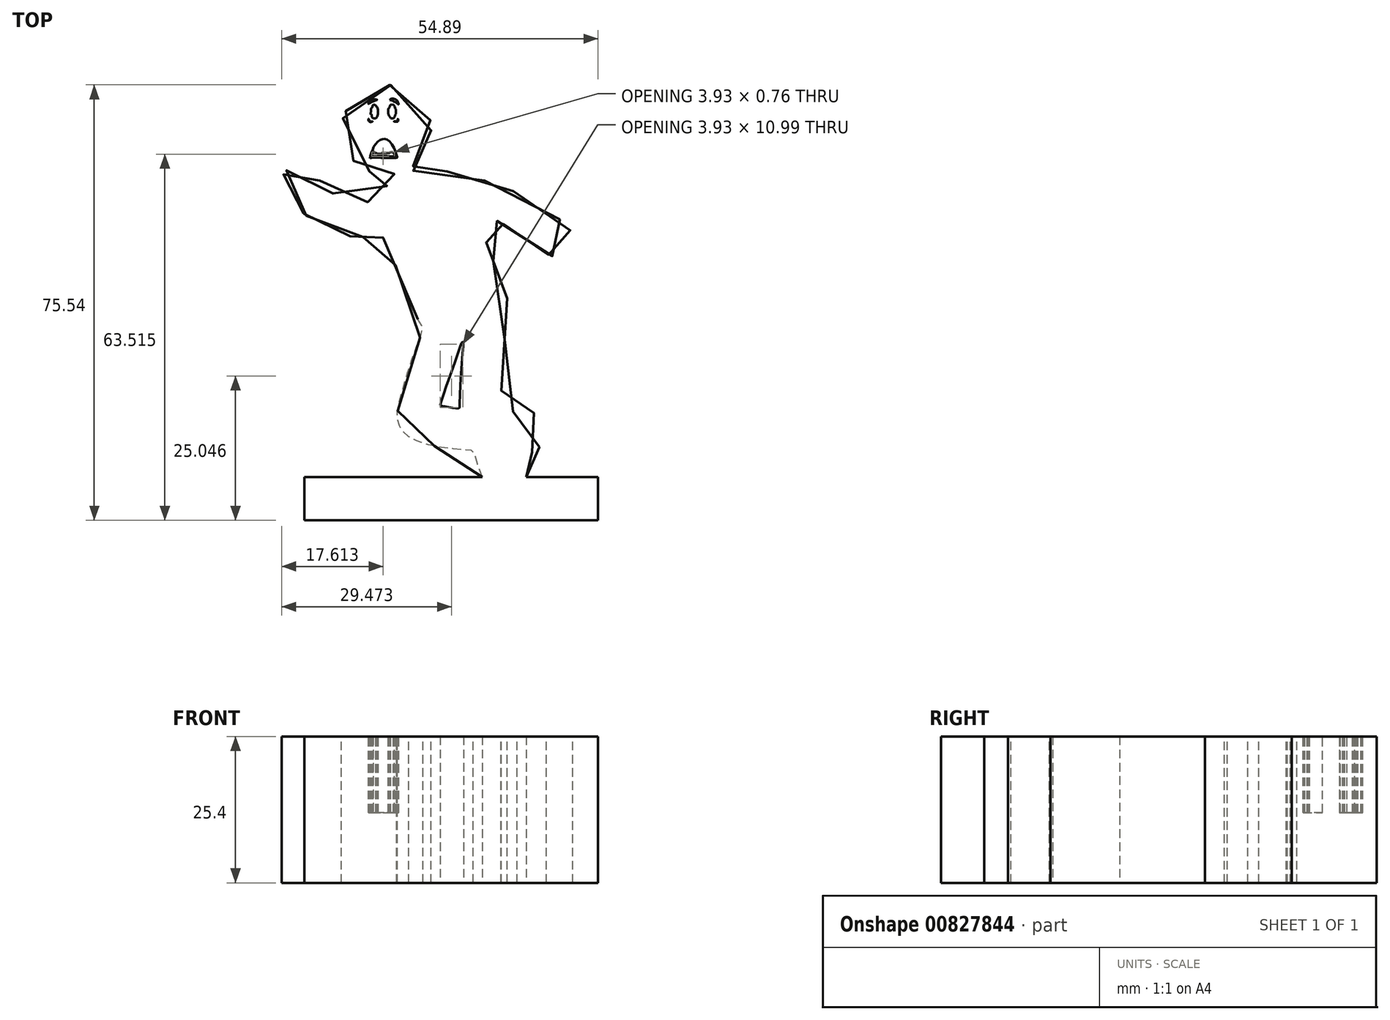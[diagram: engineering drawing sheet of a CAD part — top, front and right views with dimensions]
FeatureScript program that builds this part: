
annotation { "Feature Type Name" : "Feature", "Feature Type Description" : "" }
export const myFeature = defineFeature(function(context is Context, id is Id, definition is map)
    precondition{}
    {
        {
            var Q0;
            Q0=qCreatedBy(makeId("Top.planeOp"),FACE);
            var sketch = newSketch(context, id + "F0", { "sketchPlane" : qUnion([Q0])});
            skFitSpline(sketch, "E0", {"points": [v(-34.43, 17.8) * mm, v(-33.8, 19.88) * mm, v(-32.72, 23) * mm, v(-31.12, 27.5) * mm, v(-30.7, 28.65) * mm, v(-30.46, 28.82) * mm, v(-30.5, 27.56) * mm, v(-30.92, 21.8) * mm, v(-31.06, 17.6) * mm, v(-31.12, 17.25) * mm, v(-31.55, 17.25) * mm, v(-34.17, 17.65) * mm, v(-34.46, 17.72) * mm, v(-34.45, 17.74) * mm, v(-34.43, 17.78) * mm, v(-34.43, 17.8) * mm]});
            skFitSpline(sketch, "E1", {"points": [v(-21.09, 9.56) * mm, v(-20.18, 7) * mm, v(-19.25, 4.29) * mm, v(-19.41, 2.26) * mm, v(-20.88, 0.48) * mm, v(-22.42, 0) * mm, v(-24.42, 0.37) * mm, v(-25.78, 1.51) * mm, v(-26.8, 4.26) * mm, v(-28.3, 8.68) * mm, v(-28.7, 9.9) * mm, v(-29.32, 9.99) * mm, v(-31.53, 10.19) * mm, v(-35.27, 10.68) * mm, v(-38.95, 11.8) * mm, v(-40.4, 12.75) * mm, v(-41.25, 13.76) * mm, v(-41.78, 15.03) * mm, v(-41.86, 16.4) * mm, v(-41.72, 17.56) * mm, v(-40.92, 20.58) * mm, v(-40.26, 22.95) * mm, v(-38.55, 27.93) * mm, v(-37.54, 30.8) * mm, v(-37.48, 31.16) * mm, v(-37.45, 31.38) * mm, v(-37.89, 31.95) * mm, v(-38.71, 33.7) * mm, v(-42.6, 43) * mm, v(-44.25, 46.66) * mm, v(-44.57, 47.49) * mm, v(-44.86, 47.49) * mm, v(-45.4, 47.38) * mm, v(-45.94, 47.24) * mm, v(-46.3, 47.1) * mm, v(-48.1, 46.98) * mm, v(-50.44, 47.16) * mm, v(-52.24, 47.63) * mm, v(-53.94, 48.3) * mm, v(-56.24, 49.65) * mm, v(-58.44, 51.35) * mm, v(-60.2, 53.34) * mm, v(-61.6, 55.05) * mm, v(-61.87, 56) * mm, v(-61.87, 57.27) * mm, v(-61.11, 58.54) * mm, v(-60.17, 59.28) * mm, v(-58.54, 59.53) * mm, v(-57.12, 59.05) * mm, v(-55.31, 56.76) * mm, v(-53.1, 54.57) * mm, v(-51.22, 53.6) * mm, v(-49.05, 53.02) * mm, v(-46.71, 53.1) * mm, v(-45, 54.06) * mm, v(-43.3, 56.33) * mm, v(-42.57, 56.9) * mm, v(-41.97, 57.34) * mm, v(-42.34, 57.9) * mm, v(-42.55, 57.82) * mm, v(-43.4, 57.75) * mm, v(-45.08, 57.84) * mm, v(-46.6, 58.3) * mm, v(-48.82, 59.6) * mm, v(-50.7, 61.94) * mm, v(-51.53, 64.44) * mm, v(-51.5, 66.62) * mm, v(-51.06, 68.33) * mm, v(-49.91, 70.34) * mm, v(-48.04, 72.06) * mm, v(-46.07, 73) * mm, v(-43.55, 73.38) * mm, v(-41.12, 72.92) * mm, v(-38.67, 71.45) * mm, v(-36.76, 69.07) * mm, v(-36.06, 66.72) * mm, v(-36.04, 64.75) * mm, v(-36.33, 63.02) * mm, v(-37.79, 60.48) * mm, v(-39.33, 59.1) * mm, v(-39.87, 58.8) * mm, v(-39.36, 58.42) * mm, v(-38.99, 58.51) * mm, v(-37.05, 58.68) * mm, v(-34.13, 58.51) * mm, v(-30.46, 57.82) * mm, v(-26.68, 56.71) * mm, v(-23, 55.43) * mm, v(-18.6, 53.35) * mm, v(-14.93, 50.93) * mm, v(-12.28, 48.7) * mm, v(-11.48, 46.97) * mm, v(-11.89, 45.14) * mm, v(-12.8, 44.16) * mm, v(-13.4, 43.82) * mm, v(-15, 43.68) * mm, v(-16.8, 44.7) * mm, v(-18.07, 45.77) * mm, v(-19.6, 46.97) * mm, v(-22.71, 48.83) * mm, v(-26.07, 50.36) * mm, v(-28.44, 50.98) * mm, v(-28.72, 50.98) * mm, v(-26.78, 46.83) * mm, v(-25.17, 42.6) * mm, v(-23.84, 39.69) * mm, v(-22.87, 37.29) * mm, v(-22.92, 35.57) * mm, v(-23.36, 27.21) * mm, v(-23.86, 20.33) * mm, v(-23.86, 18.27) * mm, v(-23.61, 16.9) * mm, v(-21.3, 16.74) * mm, v(-18.45, 16.55) * mm, v(-16.53, 15.02) * mm, v(-16, 12.96) * mm, v(-16.4, 11.47) * mm, v(-18.02, 9.96) * mm, v(-19.27, 9.44) * mm, v(-20.16, 9.54) * mm, v(-20.78, 9.55) * mm, v(-20.97, 9.58) * mm, v(-21.03, 9.58) * mm, v(-21.09, 9.56) * mm]});
            skSolve(sketch);
        }
        {
            var Q0;
            Q0=makeQuery(id+"F0.imprint","IMPRINT",FACE,{"disambiguationData":[TD([[makeQuery(id+"F0.imprint","IMPRINT",EDGE,{"derivedFrom":sQuery(id+"F0.wireOp",EDGE,"E0")}),1.0]])]});
            extrude(context, id + "F1", {"entities" : qUnion([Q0]), "depth" : 25.4 * mm, "offsetDistance" : 25.4 * mm});
        }
        {
            var Q0;
            Q0=makeQuery(id+"F1.opExtrude","CAP_FACE",FACE,{"disambiguationData":[OSD([sQuery(id+"F0.wireOp",EDGE,"E0"),sQuery(id+"F0.wireOp",EDGE,"E1")])],"isStart":false});
            var sketch = newSketch(context, id + "F2", { "sketchPlane" : qUnion([Q0])});
            skFitSpline(sketch, "E2", {"points": [v(-46.89, 70.28) * mm, v(-46.68, 70.57) * mm, v(-46.42, 70.8) * mm, v(-45.95, 70.9) * mm, v(-45.37, 70.78) * mm, v(-45.59, 70.7) * mm, v(-45.92, 70.58) * mm, v(-46.42, 70.37) * mm, v(-46.7, 70.18) * mm, v(-46.8, 70.18) * mm, v(-46.84, 70.04) * mm, v(-46.89, 70.28) * mm]});
            skFitSpline(sketch, "E3", {"points": [v(-43.2, 70.71) * mm, v(-43.01, 70.72) * mm, v(-42.68, 70.6) * mm, v(-42.18, 70.36) * mm, v(-41.83, 70.14) * mm, v(-41.64, 70) * mm, v(-41.69, 70.24) * mm, v(-41.9, 70.61) * mm, v(-42.4, 70.93) * mm, v(-42.97, 70.92) * mm, v(-43.2, 70.71) * mm]});
            skFitSpline(sketch, "E4", {"points": [v(-43.1, 67.69) * mm, v(-43.25, 67.87) * mm, v(-43.29, 68.1) * mm, v(-43.4, 68.24) * mm, v(-43.43, 68.4) * mm, v(-43.43, 68.6) * mm, v(-43.44, 68.82) * mm, v(-43.45, 69.2) * mm, v(-43.33, 69.24) * mm, v(-43.31, 69.45) * mm, v(-43.29, 69.53) * mm, v(-43.17, 69.55) * mm, v(-43.17, 69.78) * mm, v(-43.03, 69.8) * mm, v(-43.03, 69.94) * mm, v(-42.98, 69.95) * mm, v(-42.75, 69.96) * mm, v(-42.6, 69.96) * mm, v(-42.57, 69.8) * mm, v(-42.46, 69.79) * mm, v(-42.43, 69.57) * mm, v(-42.3, 69.56) * mm, v(-42.28, 69.3) * mm, v(-42.15, 69.28) * mm, v(-42.15, 69.12) * mm, v(-42.15, 68.71) * mm, v(-42.15, 68.35) * mm, v(-42.14, 68.2) * mm, v(-42.25, 68.14) * mm, v(-42.28, 67.89) * mm, v(-42.4, 67.85) * mm, v(-42.41, 67.68) * mm, v(-42.54, 67.67) * mm, v(-42.56, 67.57) * mm, v(-42.97, 67.54) * mm, v(-43, 67.67) * mm, v(-43.1, 67.69) * mm]});
            skFitSpline(sketch, "E5", {"points": [v(-42.39, 67.06) * mm, v(-42, 67.05) * mm, v(-41.96, 67.12) * mm, v(-41.83, 67.16) * mm, v(-41.81, 67.33) * mm, v(-41.74, 67.48) * mm, v(-41.72, 67.13) * mm, v(-41.8, 67.04) * mm, v(-41.86, 66.97) * mm, v(-42.45, 67.03) * mm, v(-42.39, 67.06) * mm]});
            skFitSpline(sketch, "E6", {"points": [v(-46.84, 67.41) * mm, v(-46.8, 67.3) * mm, v(-46.64, 67.1) * mm, v(-46.52, 67.02) * mm, v(-46.15, 67.03) * mm, v(-46.38, 66.96) * mm, v(-46.63, 66.96) * mm, v(-46.73, 67) * mm, v(-46.78, 67.12) * mm, v(-46.88, 67.13) * mm, v(-46.9, 67.29) * mm, v(-46.86, 67.52) * mm, v(-46.84, 67.41) * mm]});
            skFitSpline(sketch, "E7", {"points": [v(-46.02, 67.54) * mm, v(-45.63, 67.55) * mm, v(-45.62, 67.68) * mm, v(-45.5, 67.7) * mm, v(-45.5, 67.84) * mm, v(-45.37, 67.86) * mm, v(-45.37, 68.07) * mm, v(-45.2, 68.11) * mm, v(-45.2, 68.26) * mm, v(-45.23, 68.63) * mm, v(-45.23, 68.94) * mm, v(-45.21, 69.2) * mm, v(-45.22, 69.26) * mm, v(-45.35, 69.26) * mm, v(-45.37, 69.48) * mm, v(-45.37, 69.57) * mm, v(-45.46, 69.57) * mm, v(-45.5, 69.78) * mm, v(-45.62, 69.8) * mm, v(-45.65, 69.92) * mm, v(-45.7, 69.92) * mm, v(-46, 69.92) * mm, v(-46.04, 69.91) * mm, v(-46.04, 69.81) * mm, v(-46.16, 69.8) * mm, v(-46.2, 69.74) * mm, v(-46.21, 69.53) * mm, v(-46.32, 69.52) * mm, v(-46.33, 69.44) * mm, v(-46.34, 69.24) * mm, v(-46.48, 69.23) * mm, v(-46.47, 69.07) * mm, v(-46.5, 68.36) * mm, v(-46.5, 68.25) * mm, v(-46.34, 68.22) * mm, v(-46.34, 67.88) * mm, v(-46.2, 67.8) * mm, v(-46.2, 67.71) * mm, v(-46.05, 67.7) * mm, v(-46.02, 67.54) * mm]});
            skFitSpline(sketch, "E8", {"points": [v(-46.3, 61.05) * mm, v(-46.15, 61.52) * mm, v(-45.92, 61.77) * mm, v(-45.46, 61.48) * mm, v(-44.66, 61.44) * mm, v(-43.81, 61.37) * mm, v(-42.77, 61.73) * mm, v(-42.22, 61.05) * mm, v(-42.46, 60.97) * mm, v(-46.15, 61) * mm, v(-46.3, 61.05) * mm]});
            skFitSpline(sketch, "E9", {"points": [v(-46.64, 60.64) * mm, v(-46.56, 61.13) * mm, v(-46.15, 62.16) * mm, v(-45.87, 62.8) * mm, v(-45.1, 63.67) * mm, v(-44.67, 63.92) * mm, v(-44.21, 64.01) * mm, v(-43.67, 63.9) * mm, v(-42.9, 63.2) * mm, v(-42.23, 61.9) * mm, v(-41.93, 60.93) * mm, v(-41.9, 60.73) * mm, v(-42.28, 60.7) * mm, v(-44.8, 60.71) * mm, v(-46.47, 60.7) * mm, v(-46.64, 60.64) * mm]});
            skSolve(sketch);
        }
        {
            var Q0;
            Q0=makeQuery(id+"F2.imprint","IMPRINT",FACE,{"disambiguationData":[TD([[makeQuery(id+"F2.imprint","IMPRINT",EDGE,{"derivedFrom":sQuery(id+"F2.wireOp",EDGE,"E8")}),1.0]])]});
            var Q1;
            Q1=makeQuery(id+"F2.imprint","IMPRINT",FACE,{"disambiguationData":[TD([[makeQuery(id+"F2.imprint","IMPRINT",EDGE,{"derivedFrom":sQuery(id+"F2.wireOp",EDGE,"E4")}),-1.0]])]});
            var Q2;
            Q2=makeQuery(id+"F2.imprint","IMPRINT",FACE,{"disambiguationData":[TD([[makeQuery(id+"F2.imprint","IMPRINT",EDGE,{"derivedFrom":sQuery(id+"F2.wireOp",EDGE,"E7")}),1.0]])]});
            var Q3;
            Q3=makeQuery(id+"F2.imprint","IMPRINT",FACE,{"disambiguationData":[TD([[makeQuery(id+"F2.imprint","IMPRINT",EDGE,{"derivedFrom":sQuery(id+"F2.wireOp",EDGE,"E2")}),-1.0]])]});
            var Q4;
            Q4=makeQuery(id+"F2.imprint","IMPRINT",FACE,{"disambiguationData":[TD([[makeQuery(id+"F2.imprint","IMPRINT",EDGE,{"derivedFrom":sQuery(id+"F2.wireOp",EDGE,"E3")}),1.0]])]});
            var Q5;
            Q5=makeQuery(id+"F2.imprint","IMPRINT",FACE,{"disambiguationData":[TD([[makeQuery(id+"F2.imprint","IMPRINT",EDGE,{"derivedFrom":sQuery(id+"F2.wireOp",EDGE,"E5")}),-1.0]])]});
            var Q6;
            Q6=makeQuery(id+"F2.imprint","IMPRINT",FACE,{"disambiguationData":[TD([[makeQuery(id+"F2.imprint","IMPRINT",EDGE,{"derivedFrom":sQuery(id+"F2.wireOp",EDGE,"E6")}),-1.0]])]});
            extrude(context, id + "F3", {"entities" : qUnion([Q0, Q1, Q2, Q3, Q4, Q5, Q6]), "oppositeDirection" : true, "depth" : 13.2 * mm, "offsetDistance" : 25.4 * mm});
        }
        {
            var Q0;
            Q0=qCreatedBy(makeId("Top.planeOp"),FACE);
            var sketch = newSketch(context, id + "F4", { "sketchPlane" : qUnion([Q0])});
            skLineSegment(sketch, "E10.bottom", {"start": v(-58, 5.32) * mm, "end": v(-7.05, 5.32) * mm});
            skLineSegment(sketch, "E10.top", {"start": v(-58, -2.16) * mm, "end": v(-7.05, -2.16) * mm});
            skLineSegment(sketch, "E10.left", {"start": v(-58, 5.32) * mm, "end": v(-58, -2.16) * mm});
            skLineSegment(sketch, "E10.right", {"start": v(-7.05, 5.32) * mm, "end": v(-7.05, -2.16) * mm});
            skSolve(sketch);
        }
        {
            var Q0;
            Q0=makeQuery(id+"F4.imprint","IMPRINT",FACE,{"disambiguationData":[TD([[makeQuery(id+"F4.imprint","IMPRINT",EDGE,{"derivedFrom":sQuery(id+"F4.wireOp",EDGE,"E10.bottom")}),-1.0]])]});
            extrude(context, id + "F5", {"entities" : qUnion([Q0]), "operationType" : NewBodyOperationType.ADD, "depth" : 25.4 * mm, "offsetDistance" : 25.4 * mm});
        }
    });
